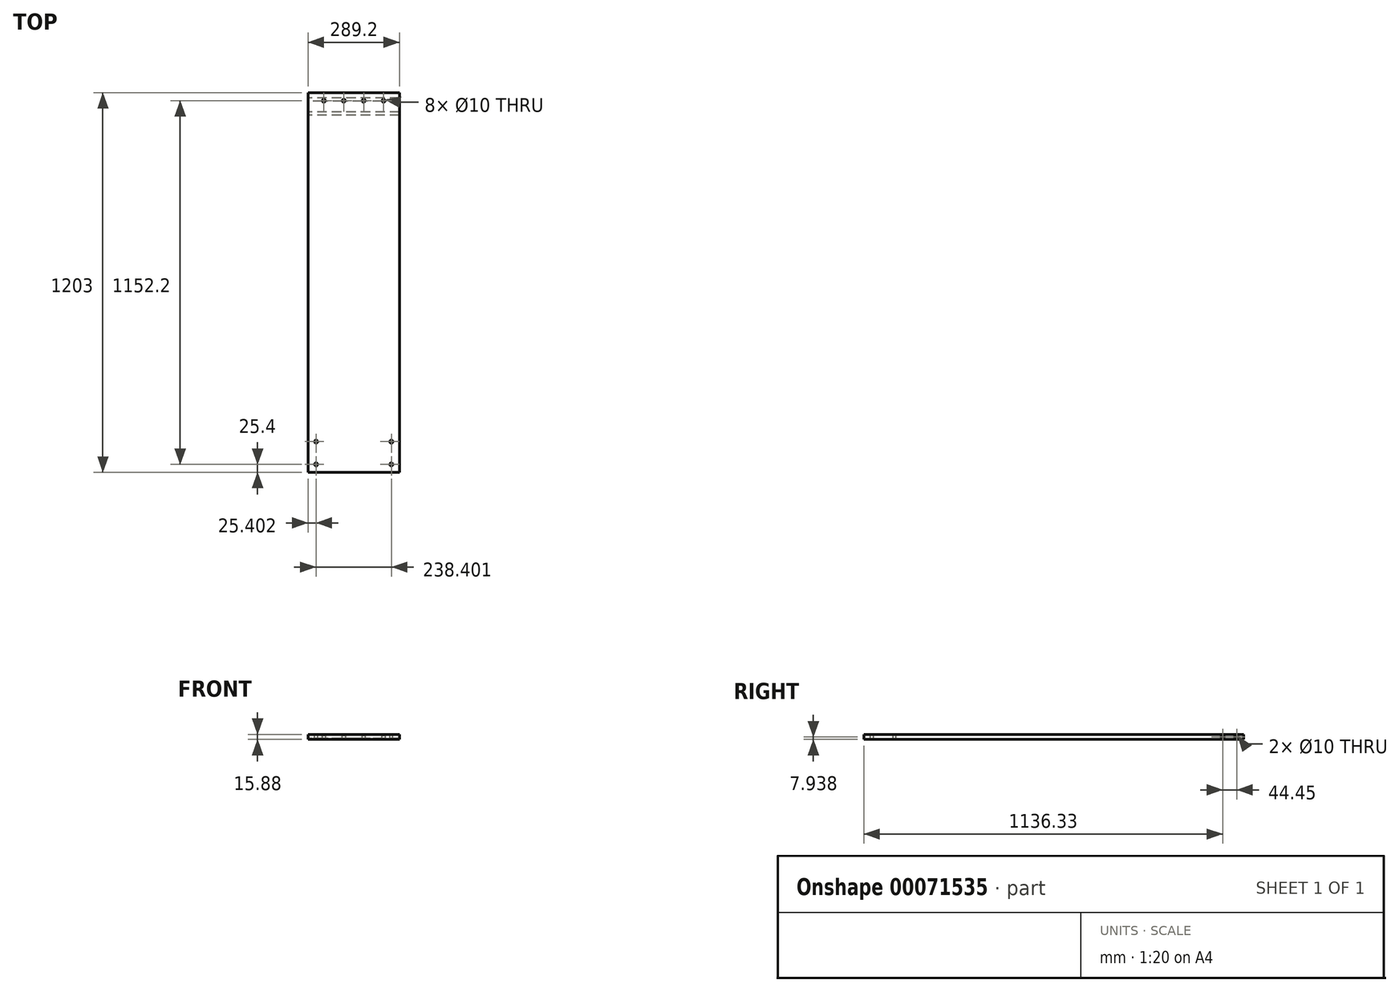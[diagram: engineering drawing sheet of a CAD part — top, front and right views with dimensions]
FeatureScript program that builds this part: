
annotation { "Feature Type Name" : "Feature", "Feature Type Description" : "" }
export const myFeature = defineFeature(function(context is Context, id is Id, definition is map)
    precondition{}
    {
        {
            var Q0;
            Q0=qCreatedBy(makeId("Front.planeOp"),FACE);
            var sketch = newSketch(context, id + "F0", { "sketchPlane" : qUnion([Q0])});
            skLineSegment(sketch, "E0.bottom", {"start": v(-15.07, 10.55) * mm, "end": v(274.13, 10.55) * mm});
            skLineSegment(sketch, "E0.top", {"start": v(-15.07, -5.33) * mm, "end": v(274.13, -5.33) * mm});
            skLineSegment(sketch, "E0.left", {"start": v(-15.07, 10.55) * mm, "end": v(-15.07, -5.33) * mm});
            skLineSegment(sketch, "E0.right", {"start": v(274.13, 10.55) * mm, "end": v(274.13, -5.33) * mm});
            skSolve(sketch);
        }
        {
            var Q0;
            Q0=qSketchRegion(id+"F0",true);
            extrude(context, id + "F1", {"entities" : qUnion([Q0]), "depth" : 1203 * mm});
        }
        {
            var Q0;
            Q0=makeQuery(id+"F1.opExtrude","SWEPT_FACE",FACE,{"disambiguationData":[OSD([sQuery(id+"F0.wireOp",EDGE,"E0.bottom")])]});
            var sketch = newSketch(context, id + "F2", { "sketchPlane" : qUnion([Q0])});
            skCircle(sketch, "E1", {"center": v(10.33, -1177.6) * mm, "radius": 5 * mm});
            skCircle(sketch, "E2", {"center": v(10.33, -1105.6) * mm, "radius": 5 * mm});
            skCircle(sketch, "E3", {"center": v(248.73, -1105.6) * mm, "radius": 5 * mm});
            skCircle(sketch, "E4", {"center": v(248.73, -1177.6) * mm, "radius": 5 * mm});
            skCircle(sketch, "E5", {"center": v(34.93, -25.4) * mm, "radius": 5 * mm});
            skCircle(sketch, "E6.1.0.0", {"center": v(98, -25.4) * mm, "radius": 5 * mm});
            skCircle(sketch, "E6.2.0.0", {"center": v(161.07, -25.4) * mm, "radius": 5 * mm});
            skCircle(sketch, "E6.3.0.0", {"center": v(224.13, -25.4) * mm, "radius": 5 * mm});
            skLineSegment(sketch, "E6.direction1", {"start": v(34.93, -25.4) * mm, "end": v(98, -25.4) * mm, "construction": true});
            skSolve(sketch);
        }
        {
            var Q0;
            Q0 = qSketchRegion(id + "F2", true);
            extrude(context, id + "F3", {"entities" : qUnion([Q0]), "operationType" : NewBodyOperationType.REMOVE, "endBound" : BoundingType.THROUGH_ALL, "oppositeDirection" : true, "depth" : 25 * mm});
        }
        {
            var Q0;
            Q0=makeQuery(id+"F1.opExtrude","SWEPT_FACE",FACE,{"disambiguationData":[OSD([sQuery(id+"F0.wireOp",EDGE,"E0.left")])]});
            var sketch = newSketch(context, id + "F4", { "sketchPlane" : qUnion([Q0])});
            skCircle(sketch, "E7", {"center": v(22.22, 2.6) * mm, "radius": 5 * mm});
            skCircle(sketch, "E8", {"center": v(66.68, 2.6) * mm, "radius": 5 * mm});
            skSolve(sketch);
        }
        {
            var Q0;
            Q0 = qSketchRegion(id + "F4", true);
            extrude(context, id + "F5", {"entities" : qUnion([Q0]), "operationType" : NewBodyOperationType.REMOVE, "endBound" : BoundingType.THROUGH_ALL, "oppositeDirection" : true, "depth" : 25 * mm});
        }
    });
